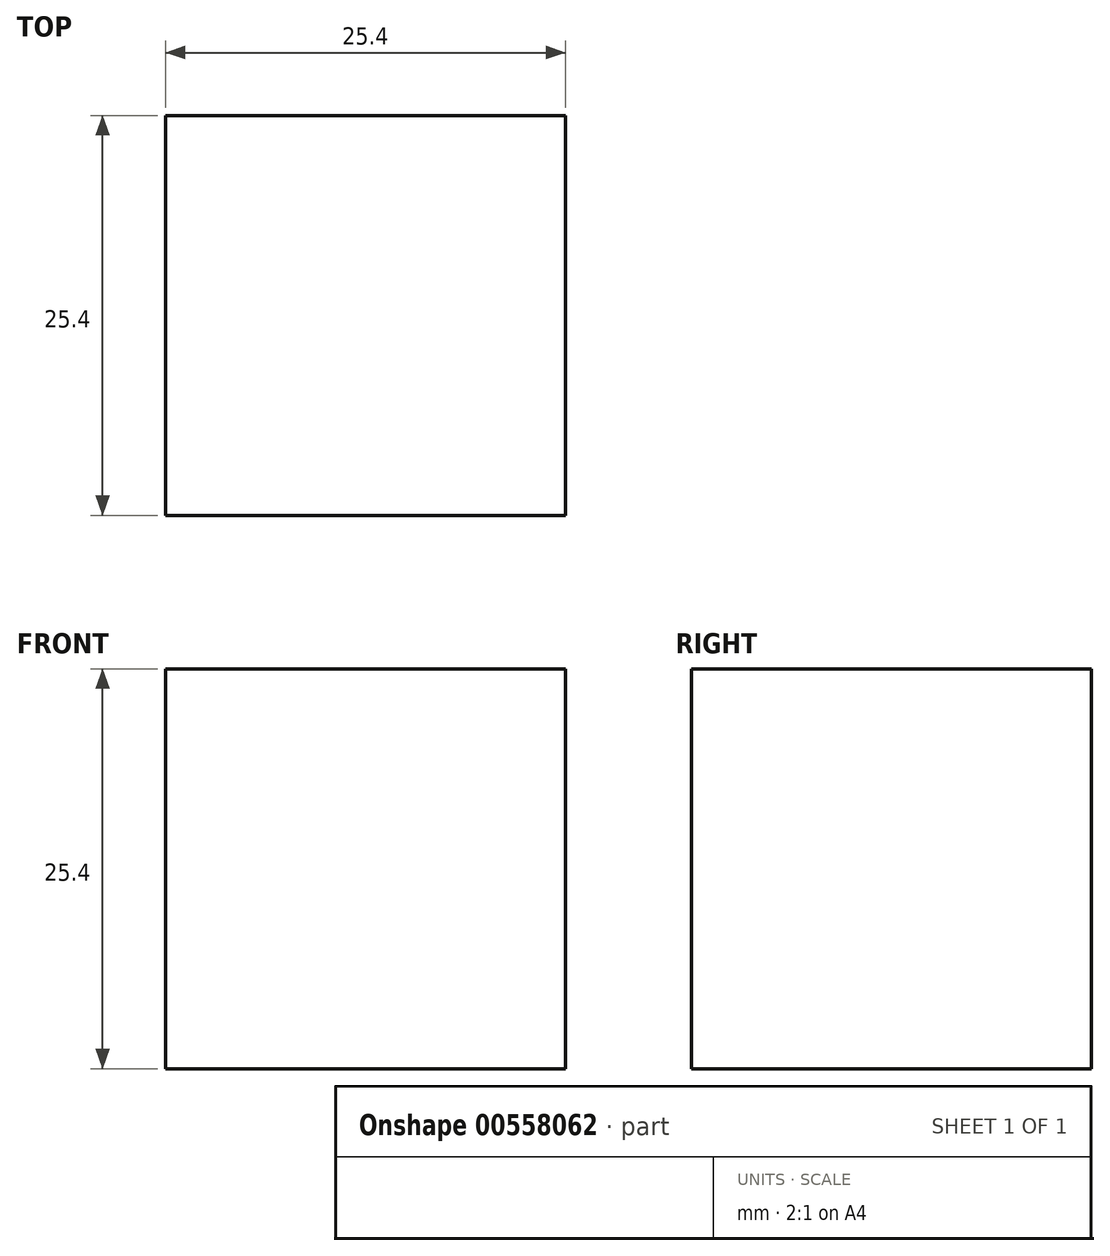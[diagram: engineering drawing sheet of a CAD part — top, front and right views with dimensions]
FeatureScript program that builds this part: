
annotation { "Feature Type Name" : "Feature", "Feature Type Description" : "" }
export const myFeature = defineFeature(function(context is Context, id is Id, definition is map)
    precondition{}
    {
        {
            var Q0;
            Q0=qCreatedBy(makeId("Right.planeOp"),FACE);
            var sketch = newSketch(context, id + "F0", { "sketchPlane" : qUnion([Q0])});
            skLineSegment(sketch, "E0", {"start": v(0, 25.4) * mm, "end": v(-25.4, 25.4) * mm});
            skLineSegment(sketch, "E1", {"start": v(-25.4, 25.4) * mm, "end": v(-25.4, 0) * mm});
            skLineSegment(sketch, "E2", {"start": v(-25.4, 0) * mm, "end": v(0, 0) * mm});
            skLineSegment(sketch, "E3", {"start": v(0, 0) * mm, "end": v(0, 25.4) * mm});
            skSolve(sketch);
        }
        {
            var Q0;
            Q0 = qSketchRegion(id + "F0", true);
            extrude(context, id + "F1", {"entities" : qUnion([Q0]), "depth" : 25.4 * mm, "offsetDistance" : 25.4 * mm});
        }
    });
